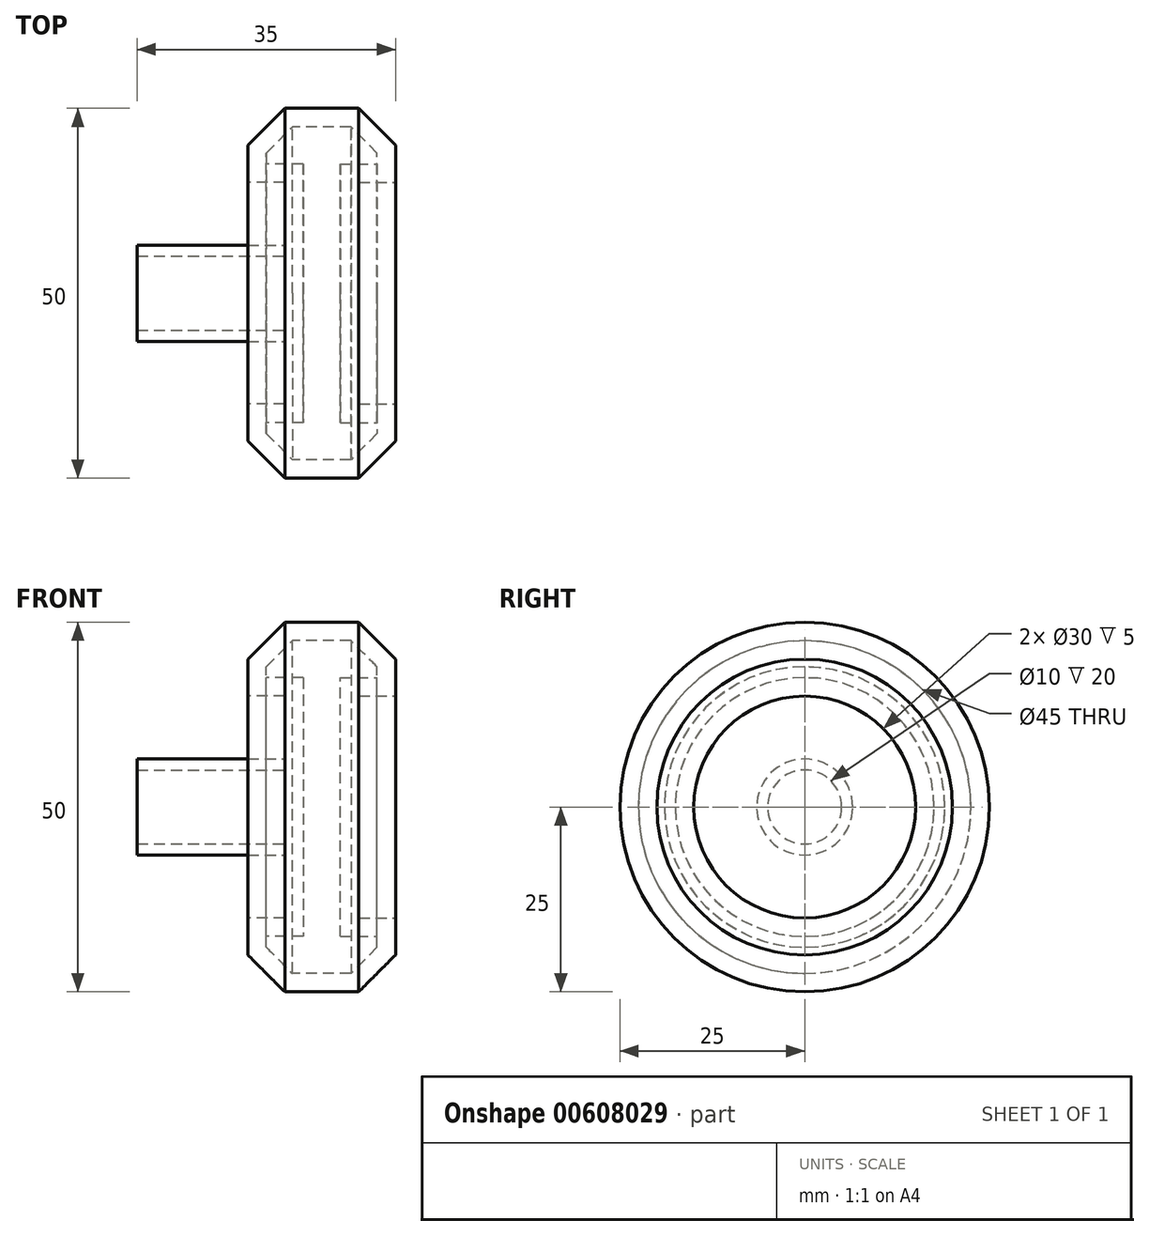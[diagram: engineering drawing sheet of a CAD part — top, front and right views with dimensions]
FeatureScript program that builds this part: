
annotation { "Feature Type Name" : "Feature", "Feature Type Description" : "" }
export const myFeature = defineFeature(function(context is Context, id is Id, definition is map)
    precondition{}
    {
        {
            var Q0;
            Q0=qCreatedBy(makeId("Right.planeOp"),FACE);
            var sketch = newSketch(context, id + "F0", { "sketchPlane" : qUnion([Q0])});
            skCircle(sketch, "E0", {"center": v(0, 0) * mm, "radius": 25 * mm});
            skSolve(sketch);
        }
        {
            var Q0;
            Q0=makeQuery(id+"F0.imprint","IMPRINT",FACE,{"disambiguationData":[TD([[makeQuery(id+"F0.imprint","IMPRINT",EDGE,{"derivedFrom":sQuery(id+"F0.wireOp",EDGE,"E0")}),1.0]])]});
            extrude(context, id + "F1", {"entities" : qUnion([Q0]), "depth" : 20 * mm, "offsetDistance" : 25 * mm});
        }
        {
            var Q0;
            Q0=makeQuery(id+"F1.opExtrude","CAP_FACE",FACE,{"disambiguationData":[OSD([sQuery(id+"F0.wireOp",EDGE,"E0")])],"isStart":false});
            chamfer(context, id + "F2", {"entities" : qUnion([Q0]), "width" : 5 * mm, "tangentPropagation" : true});
        }
        {
            var Q0;
            Q0=makeQuery(id+"F1.opExtrude","CAP_FACE",FACE,{"disambiguationData":[OSD([sQuery(id+"F0.wireOp",EDGE,"E0")])],"isStart":true});
            chamfer(context, id + "F3", {"entities" : qUnion([Q0]), "width" : 5 * mm, "tangentPropagation" : true});
        }
        {
            var Q0;
            Q0=makeQuery(id+"F1.opExtrude","CAP_FACE",FACE,{"disambiguationData":[OSD([sQuery(id+"F0.wireOp",EDGE,"E0")])],"isStart":true});
            var sketch = newSketch(context, id + "F4", { "sketchPlane" : qUnion([Q0])});
            skCircle(sketch, "E1", {"center": v(0, 0) * mm, "radius": 15 * mm});
            skSolve(sketch);
        }
        {
            var Q0;
            Q0 = qSketchRegion(id + "F4", true);
            extrude(context, id + "F5", {"entities" : qUnion([Q0]), "operationType" : NewBodyOperationType.REMOVE, "oppositeDirection" : true, "depth" : 5 * mm, "offsetDistance" : 25 * mm});
        }
        {
            var Q0;
            Q0=makeQuery(id+"F1.opExtrude","CAP_FACE",FACE,{"disambiguationData":[OSD([sQuery(id+"F0.wireOp",EDGE,"E0")])],"isStart":false});
            var sketch = newSketch(context, id + "F6", { "sketchPlane" : qUnion([Q0])});
            skCircle(sketch, "E2", {"center": v(0, 0) * mm, "radius": 15 * mm});
            skSolve(sketch);
        }
        {
            var Q0;
            Q0 = qSketchRegion(id + "F6", true);
            extrude(context, id + "F7", {"entities" : qUnion([Q0]), "operationType" : NewBodyOperationType.REMOVE, "oppositeDirection" : true, "depth" : 5 * mm, "offsetDistance" : 25 * mm});
        }
        {
            var Q0;
            Q0=makeQuery(id+"F5.boolean.opBoolean","COPY",FACE,{"derivedFrom":makeQuery(id+"F5.opExtrude","CAP_FACE",FACE,{"disambiguationData":[OSD([sQuery(id+"F4.wireOp",EDGE,"E1")])],"isStart":false})});
            var sketch = newSketch(context, id + "F8", { "sketchPlane" : qUnion([Q0])});
            skCircle(sketch, "E3", {"center": v(0, 0) * mm, "radius": 5 * mm});
            skCircle(sketch, "E4", {"center": v(0, 0) * mm, "radius": 6.5 * mm});
            skSolve(sketch);
        }
        {
            var Q0;
            Q0 = qSketchRegion(id + "F8", true);
            extrude(context, id + "F9", {"entities" : qUnion([Q0]), "operationType" : NewBodyOperationType.ADD, "depth" : 20 * mm, "offsetDistance" : 25 * mm});
        }
        {
            var Q0;
            Q0=makeQuery(id+"F9.opExtrude","CAP_FACE",FACE,{"disambiguationData":[OSD([sQuery(id+"F8.wireOp",EDGE,"E3"),sQuery(id+"F8.wireOp",EDGE,"E4")])],"isStart":false});
            shell(context, id + "F10", {"entities" : qUnion([Q0]), "thickness" : 2.5 * mm});
        }
    });
